# Revit family: Hekatron_Rauchwarnmelder_FM.Pro X_DE_22.01
name_source: partatom
category: Brandmelder
revit_build: Autodesk Revit 2018 (Build: 20190510_1515(x64)
units: mm (PartAtom-declared; Revit-internal decimal feet)

## family parameters
Basisbauteil = Fläche
Beim Laden mit Abzugskörper schneiden = Nein
Bemaßung runder Anschluss = Durchmesser verwenden
Beschriftungsausrichtung beibehalten = Ja
Gemeinsam genutzt = Nein
OmniClass-Nummer = 23.85.30.21
OmniClass-Titel = Environmental Detection/Registration
Raumberechnungspunkt = Nein
Teiletyp = Normal

## types (1)
- FM.Pro X
    Beschreibung = Funkmodul Pro X zur Funkvernetzung von Rauchwarnmeldern Genius Plus X und Genius Hx. Durch den Einsatz eines Funkmoduls Pro X wird ein Alarm flächendeckend bei allen Funk-Rauchwarnmeldern gleicher Linie und ggf. Sammelalarmlinie signalisiert. Je Linie können maximal 30 Rauchwarnmelder vernetzt werden.
    Breite (mm) = 60.0
    Funktionsprinzip = Funk
    Hersteller = Hekatron
    Höhe (mm) = 10.0
    Leistungserklärung (DoP) = CPR-31-19-003-de-en
    Link zu Ausschreibungstext = https://www.meinhplus.de
    Link zu ausschreiben.de = https://www.ausschreiben.de
    Material = PCB
    Modell = FM.Pro X
    Nettogewicht (g) = 12.0
    Tiefe (mm) = 78.0
    Typenkommentare = Funkmodul Pro X
    UB A&S Artikel Nummer = 31-5200001-12-02
    URL = https://www.hekatron-brandschutz.de
    VdS-Anerkennung = G 219068
    Version des BIM Objektes = 22.01
    Vorgabe-Ansicht = 1200 mm
    Zulässige Umgebungstemperatur = 0 °C bis + 55 °C

## geometry (parser evidence)
native form markers: Sweep x2
no freeform markers — native parametric forms only
